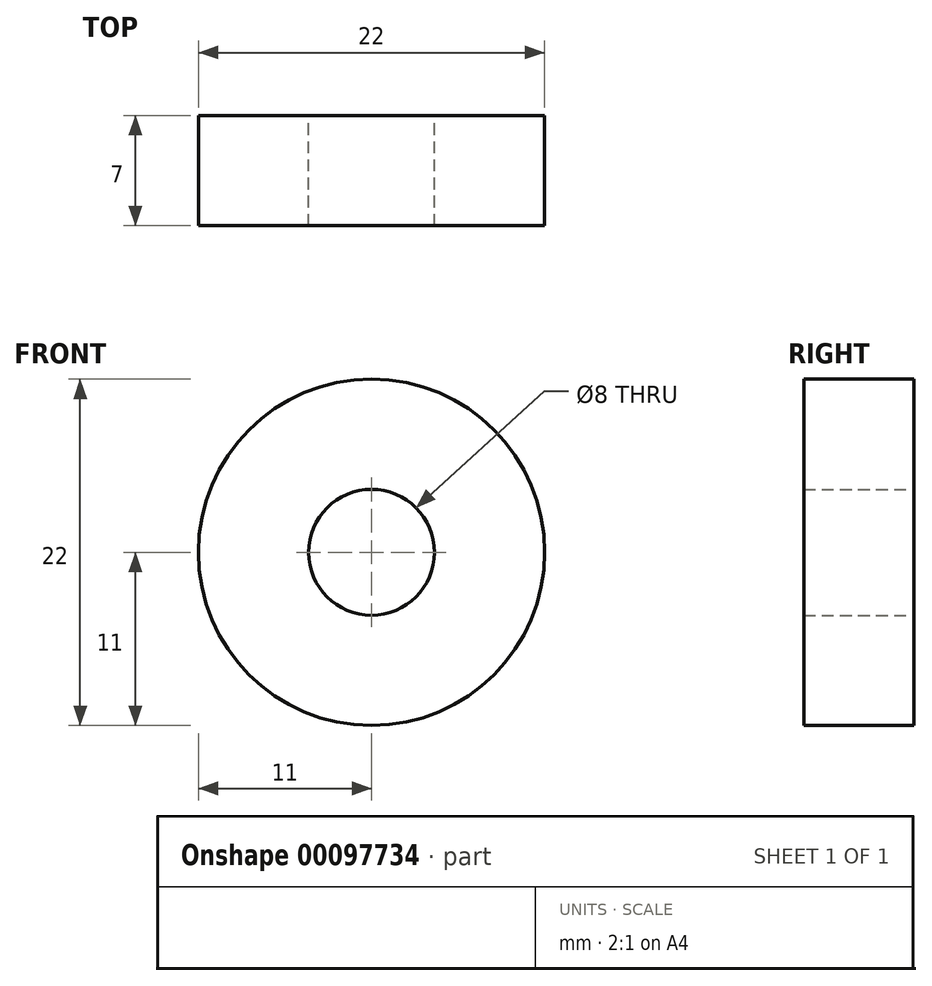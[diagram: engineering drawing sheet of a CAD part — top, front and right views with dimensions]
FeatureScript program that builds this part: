
annotation { "Feature Type Name" : "Feature", "Feature Type Description" : "" }
export const myFeature = defineFeature(function(context is Context, id is Id, definition is map)
    precondition{}
    {
        {
            var Q0;
            Q0=qCreatedBy(makeId("Front.planeOp"),FACE);
            var sketch = newSketch(context, id + "F0", { "sketchPlane" : qUnion([Q0])});
            skCircle(sketch, "E0", {"center": v(0, 0) * mm, "radius": 4 * mm});
            skCircle(sketch, "E1", {"center": v(0, 0) * mm, "radius": 11 * mm});
            skSolve(sketch);
        }
        {
            var Q0;
            Q0=makeQuery(id+"F0.imprint","IMPRINT",FACE,{"disambiguationData":[TD([[makeQuery(id+"F0.imprint","IMPRINT",EDGE,{"derivedFrom":sQuery(id+"F0.wireOp",EDGE,"E0")}),-1.0]])]});
            extrude(context, id + "F1", {"entities" : qUnion([Q0]), "endBound" : BoundingType.SYMMETRIC, "depth" : 7 * mm});
        }
    });
